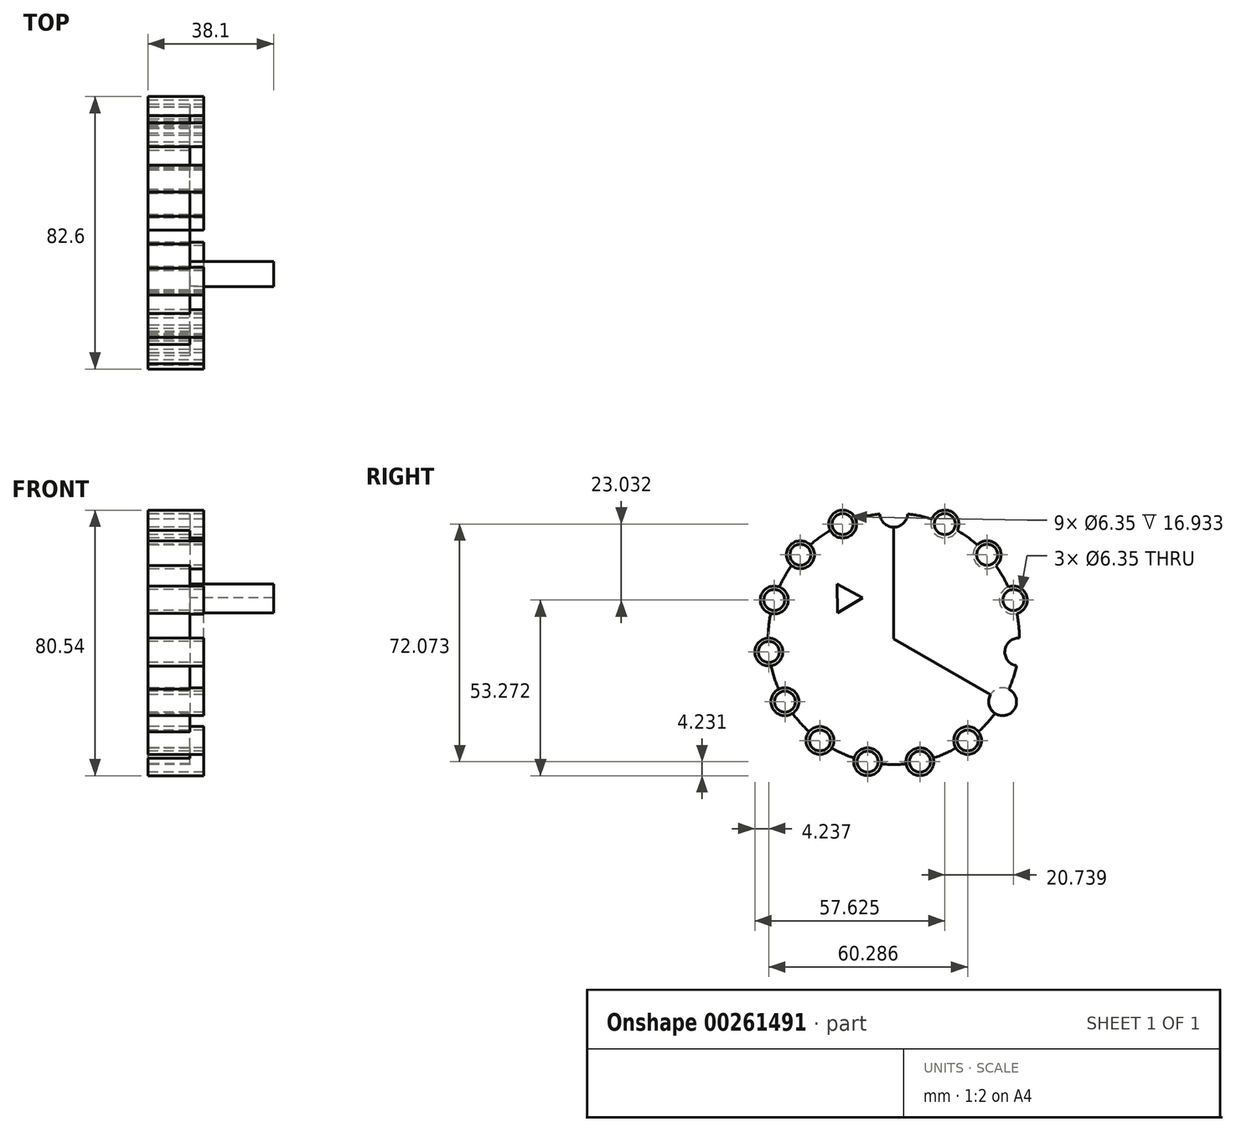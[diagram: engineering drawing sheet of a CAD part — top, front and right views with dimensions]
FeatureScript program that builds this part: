
annotation { "Feature Type Name" : "Feature", "Feature Type Description" : "" }
export const myFeature = defineFeature(function(context is Context, id is Id, definition is map)
    precondition{}
    {
        {
            var Q0;
            Q0=qCreatedBy(makeId("Right.planeOp"),FACE);
            var sketch = newSketch(context, id + "F0", { "sketchPlane" : qUnion([Q0])});
            skCircle(sketch, "E0", {"center": v(-42.41, 33.69) * mm, "radius": 38.1 * mm});
            skPoint(sketch, "E1", {"position": v(-42.41, 71.79) * mm});
            skCircle(sketch, "E2", {"center": v(-42.41, 71.79) * mm, "radius": 4.23 * mm});
            skLineSegment(sketch, "E3", {"start": v(-42.41, 33.69) * mm, "end": v(-42.41, 71.79) * mm});
            skLineSegment(sketch, "E4", {"start": v(-42.41, 33.69) * mm, "end": v(-9.42, 14.64) * mm});
            skLineSegment(sketch, "E5.MirrorCS", {"start": v(-42.41, 33.69) * mm, "end": v(-75.4, 14.64) * mm, "construction": true});
            skCircle(sketch, "E6.1.0", {"center": v(-26.91, 68.5) * mm, "radius": 4.23 * mm});
            skCircle(sketch, "E6.2.0", {"center": v(-14.1, 59.18) * mm, "radius": 4.23 * mm});
            skCircle(sketch, "E6.3.0", {"center": v(-6.18, 45.46) * mm, "radius": 4.23 * mm});
            skCircle(sketch, "E6.4.0", {"center": v(-4.52, 29.7) * mm, "radius": 4.23 * mm});
            skCircle(sketch, "E6.5.0", {"center": v(-9.42, 14.64) * mm, "radius": 4.23 * mm});
            skLineSegment(sketch, "E6.anchor1", {"start": v(-42.41, 33.69) * mm, "end": v(-42.41, 71.79) * mm, "construction": true});
            skCircle(sketch, "E7.1.0", {"center": v(-20.02, 2.86) * mm, "radius": 4.23 * mm});
            skCircle(sketch, "E7.2.0", {"center": v(-34.49, -3.58) * mm, "radius": 4.23 * mm});
            skCircle(sketch, "E7.3.0", {"center": v(-50.33, -3.58) * mm, "radius": 4.23 * mm});
            skCircle(sketch, "E7.4.0", {"center": v(-64.8, 2.86) * mm, "radius": 4.23 * mm});
            skCircle(sketch, "E7.5.0", {"center": v(-75.4, 14.64) * mm, "radius": 4.23 * mm});
            skCircle(sketch, "E8.1.0", {"center": v(-80.3, 29.7) * mm, "radius": 4.23 * mm});
            skCircle(sketch, "E8.2.0", {"center": v(-78.65, 45.46) * mm, "radius": 4.23 * mm});
            skCircle(sketch, "E8.3.0", {"center": v(-70.73, 59.18) * mm, "radius": 4.23 * mm});
            skCircle(sketch, "E8.4.0", {"center": v(-57.9, 68.5) * mm, "radius": 4.23 * mm});
            skCircle(sketch, "E9.cCircle", {"center": v(-56.97, 46.02) * mm, "radius": 2.54 * mm, "construction": true});
            skLineSegment(sketch, "E9.0", {"start": v(-59.6, 50.36) * mm, "end": v(-51.89, 46.12) * mm});
            skLineSegment(sketch, "E9.1", {"start": v(-51.89, 46.12) * mm, "end": v(-59.41, 41.57) * mm});
            skLineSegment(sketch, "E9.2", {"start": v(-59.41, 41.57) * mm, "end": v(-59.6, 50.36) * mm});
            skPoint(sketch, "E9.0.midPoint", {"position": v(-55.74, 48.24) * mm});
            skCircle(sketch, "E10", {"center": v(-6.18, 45.46) * mm, "radius": 3.18 * mm});
            skCircle(sketch, "E11.1.0", {"center": v(-4.52, 29.7) * mm, "radius": 3.18 * mm});
            skCircle(sketch, "E11.2.0", {"center": v(-9.42, 14.64) * mm, "radius": 3.17 * mm});
            skCircle(sketch, "E11.3.0", {"center": v(-20.02, 2.86) * mm, "radius": 3.18 * mm});
            skCircle(sketch, "E11.4.0", {"center": v(-34.49, -3.58) * mm, "radius": 3.18 * mm});
            skCircle(sketch, "E11.5.0", {"center": v(-50.33, -3.58) * mm, "radius": 3.18 * mm});
            skLineSegment(sketch, "E11.anchor1", {"start": v(-42.41, 33.69) * mm, "end": v(-6.18, 45.46) * mm, "construction": true});
            skLineSegment(sketch, "E11.anchor2", {"start": v(-42.41, 33.69) * mm, "end": v(-50.33, -3.58) * mm, "construction": true});
            skCircle(sketch, "E12.1.0", {"center": v(-64.8, 2.86) * mm, "radius": 3.18 * mm});
            skCircle(sketch, "E12.2.0", {"center": v(-75.4, 14.64) * mm, "radius": 3.17 * mm});
            skCircle(sketch, "E12.3.0", {"center": v(-80.3, 29.7) * mm, "radius": 3.18 * mm});
            skCircle(sketch, "E12.4.0", {"center": v(-78.65, 45.46) * mm, "radius": 3.18 * mm});
            skCircle(sketch, "E12.5.0", {"center": v(-70.73, 59.18) * mm, "radius": 3.18 * mm});
            skLineSegment(sketch, "E12.anchor2", {"start": v(-42.41, 33.69) * mm, "end": v(-70.73, 59.18) * mm, "construction": true});
            skCircle(sketch, "E13.1.0", {"center": v(-57.9, 68.5) * mm, "radius": 3.18 * mm});
            skCircle(sketch, "E13.2.0", {"center": v(-42.41, 71.79) * mm, "radius": 3.17 * mm});
            skCircle(sketch, "E13.3.0", {"center": v(-26.91, 68.5) * mm, "radius": 3.18 * mm});
            skCircle(sketch, "E13.4.0", {"center": v(-14.1, 59.18) * mm, "radius": 3.18 * mm});
            skSolve(sketch);
        }
        {
            var Q0;
            Q0=makeQuery(id+"F0.imprint","IMPRINT",FACE,{"disambiguationData":[TD([[makeQuery(id+"F0.imprint","IMPRINT",EDGE,{"derivedFrom":sQuery(id+"F0.wireOp",EDGE,"E9.0")}),1.0]])]});
            var Q1;
            {var subQ1=sQuery(id+"F0.wireOp",EDGE,"E0");var subQ4=sQuery(id+"F0.wireOp",EDGE,"E6.3.0");var subQ5=makeQuery(id+"F0.imprint","INTERSECT",VERTEX,{"disambiguationData":[OD(0.0)],"derivedFrom":[subQ1,subQ4]});Q1=makeQuery(id+"F0.imprint","IMPRINT",FACE,{"disambiguationData":[TD([[makeQuery(id+"F0.imprint","IMPRINT",EDGE,{"disambiguationData":[TD([[subQ5,1.0]])],"derivedFrom":subQ1}),1.0]])]});}
            extrude(context, id + "F1", {"entities" : qUnion([Q0, Q1]), "depth" : 12.7 * mm});
        }
        {
            var Q0;
            {var subQ0=sQuery(id+"F0.wireOp",EDGE,"E6.4.0");var subQ1=sQuery(id+"F0.wireOp",EDGE,"E0");var subQ2=makeQuery(id+"F0.imprint","INTERSECT",VERTEX,{"disambiguationData":[OD(1.0)],"derivedFrom":[subQ1,subQ0]});Q0=makeQuery(id+"F0.imprint","IMPRINT",FACE,{"disambiguationData":[TD([[makeQuery(id+"F0.imprint","IMPRINT",EDGE,{"disambiguationData":[TD([[subQ2,-1.0]])],"derivedFrom":subQ1}),1.0]])]});}
            var Q1;
            {var subQ0=sQuery(id+"F0.wireOp",EDGE,"E7.2.0");var subQ1=sQuery(id+"F0.wireOp",EDGE,"E0");var subQ2=makeQuery(id+"F0.imprint","INTERSECT",VERTEX,{"disambiguationData":[OD(0.0)],"derivedFrom":[subQ1,subQ0]});Q1=makeQuery(id+"F0.imprint","IMPRINT",FACE,{"disambiguationData":[TD([[makeQuery(id+"F0.imprint","IMPRINT",EDGE,{"disambiguationData":[TD([[subQ2,-1.0]])],"derivedFrom":subQ1}),-1.0]])]});}
            var Q2;
            {var subQ0=sQuery(id+"F0.wireOp",EDGE,"E8.1.0");var subQ1=sQuery(id+"F0.wireOp",EDGE,"E0");var subQ2=makeQuery(id+"F0.imprint","INTERSECT",VERTEX,{"disambiguationData":[OD(0.0)],"derivedFrom":[subQ1,subQ0]});Q2=makeQuery(id+"F0.imprint","IMPRINT",FACE,{"disambiguationData":[TD([[makeQuery(id+"F0.imprint","IMPRINT",EDGE,{"disambiguationData":[TD([[subQ2,-1.0]])],"derivedFrom":subQ1}),1.0]])]});}
            var Q3;
            {var subQ0=sQuery(id+"F0.wireOp",EDGE,"E6.1.0");var subQ1=sQuery(id+"F0.wireOp",EDGE,"E0");var subQ2=makeQuery(id+"F0.imprint","INTERSECT",VERTEX,{"disambiguationData":[OD(0.0)],"derivedFrom":[subQ1,subQ0]});Q3=makeQuery(id+"F0.imprint","IMPRINT",FACE,{"disambiguationData":[TD([[makeQuery(id+"F0.imprint","IMPRINT",EDGE,{"disambiguationData":[TD([[subQ2,-1.0]])],"derivedFrom":subQ1}),-1.0]])]});}
            var Q4;
            {var subQ0=sQuery(id+"F0.wireOp",EDGE,"E8.3.0");var subQ1=sQuery(id+"F0.wireOp",EDGE,"E0");var subQ2=makeQuery(id+"F0.imprint","INTERSECT",VERTEX,{"disambiguationData":[OD(0.0)],"derivedFrom":[subQ1,subQ0]});Q4=makeQuery(id+"F0.imprint","IMPRINT",FACE,{"disambiguationData":[TD([[makeQuery(id+"F0.imprint","IMPRINT",EDGE,{"disambiguationData":[TD([[subQ2,-1.0]])],"derivedFrom":subQ1}),1.0]])]});}
            var Q5;
            {var subQ0=sQuery(id+"F0.wireOp",EDGE,"E7.4.0");var subQ1=sQuery(id+"F0.wireOp",EDGE,"E0");var subQ2=makeQuery(id+"F0.imprint","INTERSECT",VERTEX,{"disambiguationData":[OD(0.0)],"derivedFrom":[subQ1,subQ0]});Q5=makeQuery(id+"F0.imprint","IMPRINT",FACE,{"disambiguationData":[TD([[makeQuery(id+"F0.imprint","IMPRINT",EDGE,{"disambiguationData":[TD([[subQ2,-1.0]])],"derivedFrom":subQ1}),1.0]])]});}
            var Q6;
            {var subQ0=sQuery(id+"F0.wireOp",EDGE,"E12.1.0");var subQ1=sQuery(id+"F0.wireOp",EDGE,"E0");var subQ2=makeQuery(id+"F0.imprint","INTERSECT",VERTEX,{"disambiguationData":[OD(0.0)],"derivedFrom":[subQ1,subQ0]});Q6=makeQuery(id+"F0.imprint","IMPRINT",FACE,{"disambiguationData":[TD([[makeQuery(id+"F0.imprint","IMPRINT",EDGE,{"disambiguationData":[TD([[subQ2,-1.0]])],"derivedFrom":subQ1}),1.0]])]});}
            var Q7;
            {var subQ0=sQuery(id+"F0.wireOp",EDGE,"E6.2.0");var subQ1=sQuery(id+"F0.wireOp",EDGE,"E0");var subQ2=makeQuery(id+"F0.imprint","INTERSECT",VERTEX,{"disambiguationData":[OD(0.0)],"derivedFrom":[subQ1,subQ0]});Q7=makeQuery(id+"F0.imprint","IMPRINT",FACE,{"disambiguationData":[TD([[makeQuery(id+"F0.imprint","IMPRINT",EDGE,{"disambiguationData":[TD([[subQ2,-1.0]])],"derivedFrom":subQ1}),-1.0]])]});}
            var Q8;
            {var subQ0=sQuery(id+"F0.wireOp",EDGE,"E6.5.0");var subQ1=sQuery(id+"F0.wireOp",EDGE,"E0");var subQ2=makeQuery(id+"F0.imprint","INTERSECT",VERTEX,{"disambiguationData":[OD(0.0)],"derivedFrom":[subQ1,subQ0]});Q8=makeQuery(id+"F0.imprint","IMPRINT",FACE,{"disambiguationData":[TD([[makeQuery(id+"F0.imprint","IMPRINT",EDGE,{"disambiguationData":[TD([[subQ2,-1.0]])],"derivedFrom":subQ1}),1.0]])]});}
            var Q9;
            {var subQ0=sQuery(id+"F0.wireOp",EDGE,"E6.4.0");var subQ1=sQuery(id+"F0.wireOp",EDGE,"E0");var subQ2=makeQuery(id+"F0.imprint","INTERSECT",VERTEX,{"disambiguationData":[OD(1.0)],"derivedFrom":[subQ1,subQ0]});Q9=makeQuery(id+"F0.imprint","IMPRINT",FACE,{"disambiguationData":[TD([[makeQuery(id+"F0.imprint","IMPRINT",EDGE,{"disambiguationData":[TD([[subQ2,-1.0]])],"derivedFrom":subQ1}),-1.0]])]});}
            var Q10;
            {var subQ0=sQuery(id+"F0.wireOp",EDGE,"E8.2.0");var subQ1=sQuery(id+"F0.wireOp",EDGE,"E0");var subQ2=makeQuery(id+"F0.imprint","INTERSECT",VERTEX,{"disambiguationData":[OD(0.0)],"derivedFrom":[subQ1,subQ0]});Q10=makeQuery(id+"F0.imprint","IMPRINT",FACE,{"disambiguationData":[TD([[makeQuery(id+"F0.imprint","IMPRINT",EDGE,{"disambiguationData":[TD([[subQ2,-1.0]])],"derivedFrom":subQ1}),1.0]])]});}
            var Q11;
            {var subQ0=sQuery(id+"F0.wireOp",EDGE,"E2");var subQ1=sQuery(id+"F0.wireOp",EDGE,"E0");var subQ2=makeQuery(id+"F0.imprint","INTERSECT",VERTEX,{"disambiguationData":[OD(0.0)],"derivedFrom":[subQ1,subQ0]});Q11=makeQuery(id+"F0.imprint","IMPRINT",FACE,{"disambiguationData":[TD([[makeQuery(id+"F0.imprint","IMPRINT",EDGE,{"disambiguationData":[TD([[subQ2,-1.0]])],"derivedFrom":subQ1}),1.0]])]});}
            var Q12;
            {var subQ0=sQuery(id+"F0.wireOp",EDGE,"E7.3.0");var subQ1=sQuery(id+"F0.wireOp",EDGE,"E0");var subQ2=makeQuery(id+"F0.imprint","INTERSECT",VERTEX,{"disambiguationData":[OD(0.0)],"derivedFrom":[subQ1,subQ0]});Q12=makeQuery(id+"F0.imprint","IMPRINT",FACE,{"disambiguationData":[TD([[makeQuery(id+"F0.imprint","IMPRINT",EDGE,{"disambiguationData":[TD([[subQ2,-1.0]])],"derivedFrom":subQ1}),1.0]])]});}
            var Q13;
            {var subQ0=sQuery(id+"F0.wireOp",EDGE,"E6.3.0");var subQ1=sQuery(id+"F0.wireOp",EDGE,"E0");var subQ2=makeQuery(id+"F0.imprint","INTERSECT",VERTEX,{"disambiguationData":[OD(0.0)],"derivedFrom":[subQ1,subQ0]});Q13=makeQuery(id+"F0.imprint","IMPRINT",FACE,{"disambiguationData":[TD([[makeQuery(id+"F0.imprint","IMPRINT",EDGE,{"disambiguationData":[TD([[subQ2,-1.0]])],"derivedFrom":subQ1}),1.0]])]});}
            var Q14;
            {var subQ0=sQuery(id+"F0.wireOp",EDGE,"E11.5.0");var subQ1=sQuery(id+"F0.wireOp",EDGE,"E0");var subQ2=makeQuery(id+"F0.imprint","INTERSECT",VERTEX,{"disambiguationData":[OD(0.0)],"derivedFrom":[subQ1,subQ0]});Q14=makeQuery(id+"F0.imprint","IMPRINT",FACE,{"disambiguationData":[TD([[makeQuery(id+"F0.imprint","IMPRINT",EDGE,{"disambiguationData":[TD([[subQ2,-1.0]])],"derivedFrom":subQ1}),1.0]])]});}
            var Q15;
            {var subQ0=sQuery(id+"F0.wireOp",EDGE,"E7.4.0");var subQ1=sQuery(id+"F0.wireOp",EDGE,"E0");var subQ2=makeQuery(id+"F0.imprint","INTERSECT",VERTEX,{"disambiguationData":[OD(0.0)],"derivedFrom":[subQ1,subQ0]});Q15=makeQuery(id+"F0.imprint","IMPRINT",FACE,{"disambiguationData":[TD([[makeQuery(id+"F0.imprint","IMPRINT",EDGE,{"disambiguationData":[TD([[subQ2,-1.0]])],"derivedFrom":subQ1}),-1.0]])]});}
            var Q16;
            {var subQ0=sQuery(id+"F0.wireOp",EDGE,"E8.1.0");var subQ1=sQuery(id+"F0.wireOp",EDGE,"E0");var subQ2=makeQuery(id+"F0.imprint","INTERSECT",VERTEX,{"disambiguationData":[OD(0.0)],"derivedFrom":[subQ1,subQ0]});Q16=makeQuery(id+"F0.imprint","IMPRINT",FACE,{"disambiguationData":[TD([[makeQuery(id+"F0.imprint","IMPRINT",EDGE,{"disambiguationData":[TD([[subQ2,-1.0]])],"derivedFrom":subQ1}),-1.0]])]});}
            var Q17;
            {var subQ0=sQuery(id+"F0.wireOp",EDGE,"E11.1.0");var subQ1=sQuery(id+"F0.wireOp",EDGE,"E0");var subQ2=makeQuery(id+"F0.imprint","INTERSECT",VERTEX,{"disambiguationData":[OD(0.0)],"derivedFrom":[subQ1,subQ0]});Q17=makeQuery(id+"F0.imprint","IMPRINT",FACE,{"disambiguationData":[TD([[makeQuery(id+"F0.imprint","IMPRINT",EDGE,{"disambiguationData":[TD([[subQ2,-1.0]])],"derivedFrom":subQ1}),1.0]])]});}
            var Q18;
            {var subQ0=sQuery(id+"F0.wireOp",EDGE,"E8.3.0");var subQ1=sQuery(id+"F0.wireOp",EDGE,"E0");var subQ2=makeQuery(id+"F0.imprint","INTERSECT",VERTEX,{"disambiguationData":[OD(0.0)],"derivedFrom":[subQ1,subQ0]});Q18=makeQuery(id+"F0.imprint","IMPRINT",FACE,{"disambiguationData":[TD([[makeQuery(id+"F0.imprint","IMPRINT",EDGE,{"disambiguationData":[TD([[subQ2,-1.0]])],"derivedFrom":subQ1}),-1.0]])]});}
            var Q19;
            {var subQ0=sQuery(id+"F0.wireOp",EDGE,"E7.2.0");var subQ1=sQuery(id+"F0.wireOp",EDGE,"E0");var subQ2=makeQuery(id+"F0.imprint","INTERSECT",VERTEX,{"disambiguationData":[OD(0.0)],"derivedFrom":[subQ1,subQ0]});Q19=makeQuery(id+"F0.imprint","IMPRINT",FACE,{"disambiguationData":[TD([[makeQuery(id+"F0.imprint","IMPRINT",EDGE,{"disambiguationData":[TD([[subQ2,-1.0]])],"derivedFrom":subQ1}),1.0]])]});}
            var Q20;
            {var subQ0=sQuery(id+"F0.wireOp",EDGE,"E7.5.0");var subQ1=sQuery(id+"F0.wireOp",EDGE,"E0");var subQ2=makeQuery(id+"F0.imprint","INTERSECT",VERTEX,{"disambiguationData":[OD(0.0)],"derivedFrom":[subQ1,subQ0]});Q20=makeQuery(id+"F0.imprint","IMPRINT",FACE,{"disambiguationData":[TD([[makeQuery(id+"F0.imprint","IMPRINT",EDGE,{"disambiguationData":[TD([[subQ2,-1.0]])],"derivedFrom":subQ1}),1.0]])]});}
            var Q21;
            {var subQ0=sQuery(id+"F0.wireOp",EDGE,"E12.3.0");var subQ1=sQuery(id+"F0.wireOp",EDGE,"E0");var subQ2=makeQuery(id+"F0.imprint","INTERSECT",VERTEX,{"disambiguationData":[OD(0.0)],"derivedFrom":[subQ1,subQ0]});Q21=makeQuery(id+"F0.imprint","IMPRINT",FACE,{"disambiguationData":[TD([[makeQuery(id+"F0.imprint","IMPRINT",EDGE,{"disambiguationData":[TD([[subQ2,-1.0]])],"derivedFrom":subQ1}),1.0]])]});}
            var Q22;
            {var subQ0=sQuery(id+"F0.wireOp",EDGE,"E13.1.0");var subQ1=sQuery(id+"F0.wireOp",EDGE,"E0");var subQ2=makeQuery(id+"F0.imprint","INTERSECT",VERTEX,{"disambiguationData":[OD(0.0)],"derivedFrom":[subQ1,subQ0]});Q22=makeQuery(id+"F0.imprint","IMPRINT",FACE,{"disambiguationData":[TD([[makeQuery(id+"F0.imprint","IMPRINT",EDGE,{"disambiguationData":[TD([[subQ2,-1.0]])],"derivedFrom":subQ1}),1.0]])]});}
            var Q23;
            {var subQ0=sQuery(id+"F0.wireOp",EDGE,"E6.1.0");var subQ1=sQuery(id+"F0.wireOp",EDGE,"E0");var subQ2=makeQuery(id+"F0.imprint","INTERSECT",VERTEX,{"disambiguationData":[OD(0.0)],"derivedFrom":[subQ1,subQ0]});Q23=makeQuery(id+"F0.imprint","IMPRINT",FACE,{"disambiguationData":[TD([[makeQuery(id+"F0.imprint","IMPRINT",EDGE,{"disambiguationData":[TD([[subQ2,-1.0]])],"derivedFrom":subQ1}),1.0]])]});}
            var Q24;
            {var subQ0=sQuery(id+"F0.wireOp",EDGE,"E7.3.0");var subQ1=sQuery(id+"F0.wireOp",EDGE,"E0");var subQ2=makeQuery(id+"F0.imprint","INTERSECT",VERTEX,{"disambiguationData":[OD(0.0)],"derivedFrom":[subQ1,subQ0]});Q24=makeQuery(id+"F0.imprint","IMPRINT",FACE,{"disambiguationData":[TD([[makeQuery(id+"F0.imprint","IMPRINT",EDGE,{"disambiguationData":[TD([[subQ2,-1.0]])],"derivedFrom":subQ1}),-1.0]])]});}
            var Q25;
            {var subQ0=sQuery(id+"F0.wireOp",EDGE,"E12.1.0");var subQ1=sQuery(id+"F0.wireOp",EDGE,"E0");var subQ2=makeQuery(id+"F0.imprint","INTERSECT",VERTEX,{"disambiguationData":[OD(0.0)],"derivedFrom":[subQ1,subQ0]});Q25=makeQuery(id+"F0.imprint","IMPRINT",FACE,{"disambiguationData":[TD([[makeQuery(id+"F0.imprint","IMPRINT",EDGE,{"disambiguationData":[TD([[subQ2,-1.0]])],"derivedFrom":subQ1}),-1.0]])]});}
            var Q26;
            {var subQ0=sQuery(id+"F0.wireOp",EDGE,"E6.2.0");var subQ1=sQuery(id+"F0.wireOp",EDGE,"E0");var subQ2=makeQuery(id+"F0.imprint","INTERSECT",VERTEX,{"disambiguationData":[OD(0.0)],"derivedFrom":[subQ1,subQ0]});Q26=makeQuery(id+"F0.imprint","IMPRINT",FACE,{"disambiguationData":[TD([[makeQuery(id+"F0.imprint","IMPRINT",EDGE,{"disambiguationData":[TD([[subQ2,-1.0]])],"derivedFrom":subQ1}),1.0]])]});}
            var Q27;
            {var subQ0=sQuery(id+"F0.wireOp",EDGE,"E7.1.0");var subQ1=sQuery(id+"F0.wireOp",EDGE,"E0");var subQ2=makeQuery(id+"F0.imprint","INTERSECT",VERTEX,{"disambiguationData":[OD(0.0)],"derivedFrom":[subQ1,subQ0]});Q27=makeQuery(id+"F0.imprint","IMPRINT",FACE,{"disambiguationData":[TD([[makeQuery(id+"F0.imprint","IMPRINT",EDGE,{"disambiguationData":[TD([[subQ2,-1.0]])],"derivedFrom":subQ1}),-1.0]])]});}
            var Q28;
            {var subQ0=sQuery(id+"F0.wireOp",EDGE,"E12.5.0");var subQ1=sQuery(id+"F0.wireOp",EDGE,"E0");var subQ2=makeQuery(id+"F0.imprint","INTERSECT",VERTEX,{"disambiguationData":[OD(0.0)],"derivedFrom":[subQ1,subQ0]});Q28=makeQuery(id+"F0.imprint","IMPRINT",FACE,{"disambiguationData":[TD([[makeQuery(id+"F0.imprint","IMPRINT",EDGE,{"disambiguationData":[TD([[subQ2,-1.0]])],"derivedFrom":subQ1}),-1.0]])]});}
            var Q29;
            {var subQ0=sQuery(id+"F0.wireOp",EDGE,"E7.1.0");var subQ1=sQuery(id+"F0.wireOp",EDGE,"E0");var subQ2=makeQuery(id+"F0.imprint","INTERSECT",VERTEX,{"disambiguationData":[OD(0.0)],"derivedFrom":[subQ1,subQ0]});Q29=makeQuery(id+"F0.imprint","IMPRINT",FACE,{"disambiguationData":[TD([[makeQuery(id+"F0.imprint","IMPRINT",EDGE,{"disambiguationData":[TD([[subQ2,-1.0]])],"derivedFrom":subQ1}),1.0]])]});}
            var Q30;
            {var subQ0=sQuery(id+"F0.wireOp",EDGE,"E6.3.0");var subQ1=sQuery(id+"F0.wireOp",EDGE,"E0");var subQ2=makeQuery(id+"F0.imprint","INTERSECT",VERTEX,{"disambiguationData":[OD(0.0)],"derivedFrom":[subQ1,subQ0]});Q30=makeQuery(id+"F0.imprint","IMPRINT",FACE,{"disambiguationData":[TD([[makeQuery(id+"F0.imprint","IMPRINT",EDGE,{"disambiguationData":[TD([[subQ2,-1.0]])],"derivedFrom":subQ1}),-1.0]])]});}
            var Q31;
            {var subQ0=sQuery(id+"F0.wireOp",EDGE,"E7.5.0");var subQ1=sQuery(id+"F0.wireOp",EDGE,"E0");var subQ2=makeQuery(id+"F0.imprint","INTERSECT",VERTEX,{"disambiguationData":[OD(0.0)],"derivedFrom":[subQ1,subQ0]});Q31=makeQuery(id+"F0.imprint","IMPRINT",FACE,{"disambiguationData":[TD([[makeQuery(id+"F0.imprint","IMPRINT",EDGE,{"disambiguationData":[TD([[subQ2,-1.0]])],"derivedFrom":subQ1}),-1.0]])]});}
            var Q32;
            Q32=makeQuery(id+"F0.imprint","IMPRINT",FACE,{"disambiguationData":[TD([[makeQuery(id+"F0.imprint","IMPRINT",EDGE,{"derivedFrom":sQuery(id+"F0.wireOp",EDGE,"E9.0")}),-1.0]])]});
            var Q33;
            {var subQ0=sQuery(id+"F0.wireOp",EDGE,"E8.4.0");var subQ1=sQuery(id+"F0.wireOp",EDGE,"E0");var subQ2=makeQuery(id+"F0.imprint","INTERSECT",VERTEX,{"disambiguationData":[OD(0.0)],"derivedFrom":[subQ1,subQ0]});Q33=makeQuery(id+"F0.imprint","IMPRINT",FACE,{"disambiguationData":[TD([[makeQuery(id+"F0.imprint","IMPRINT",EDGE,{"disambiguationData":[TD([[subQ2,-1.0]])],"derivedFrom":subQ1}),-1.0]])]});}
            var Q34;
            {var subQ0=sQuery(id+"F0.wireOp",EDGE,"E6.5.0");var subQ1=sQuery(id+"F0.wireOp",EDGE,"E0");var subQ2=makeQuery(id+"F0.imprint","INTERSECT",VERTEX,{"disambiguationData":[OD(0.0)],"derivedFrom":[subQ1,subQ0]});Q34=makeQuery(id+"F0.imprint","IMPRINT",FACE,{"disambiguationData":[TD([[makeQuery(id+"F0.imprint","IMPRINT",EDGE,{"disambiguationData":[TD([[subQ2,-1.0]])],"derivedFrom":subQ1}),-1.0]])]});}
            var Q35;
            {var subQ0=sQuery(id+"F0.wireOp",EDGE,"E11.5.0");var subQ1=sQuery(id+"F0.wireOp",EDGE,"E0");var subQ2=makeQuery(id+"F0.imprint","INTERSECT",VERTEX,{"disambiguationData":[OD(0.0)],"derivedFrom":[subQ1,subQ0]});Q35=makeQuery(id+"F0.imprint","IMPRINT",FACE,{"disambiguationData":[TD([[makeQuery(id+"F0.imprint","IMPRINT",EDGE,{"disambiguationData":[TD([[subQ2,-1.0]])],"derivedFrom":subQ1}),-1.0]])]});}
            var Q36;
            {var subQ0=sQuery(id+"F0.wireOp",EDGE,"E6.5.0");var subQ1=sQuery(id+"F0.wireOp",EDGE,"E0");var subQ2=makeQuery(id+"F0.imprint","INTERSECT",VERTEX,{"disambiguationData":[OD(1.0)],"derivedFrom":[subQ1,subQ0]});Q36=makeQuery(id+"F0.imprint","IMPRINT",FACE,{"disambiguationData":[TD([[makeQuery(id+"F0.imprint","IMPRINT",EDGE,{"disambiguationData":[TD([[subQ2,1.0]])],"derivedFrom":subQ1}),1.0]])]});}
            var Q37;
            {var subQ0=sQuery(id+"F0.wireOp",EDGE,"E8.2.0");var subQ1=sQuery(id+"F0.wireOp",EDGE,"E0");var subQ2=makeQuery(id+"F0.imprint","INTERSECT",VERTEX,{"disambiguationData":[OD(0.0)],"derivedFrom":[subQ1,subQ0]});Q37=makeQuery(id+"F0.imprint","IMPRINT",FACE,{"disambiguationData":[TD([[makeQuery(id+"F0.imprint","IMPRINT",EDGE,{"disambiguationData":[TD([[subQ2,-1.0]])],"derivedFrom":subQ1}),-1.0]])]});}
            var Q38;
            {var subQ0=sQuery(id+"F0.wireOp",EDGE,"E8.4.0");var subQ1=sQuery(id+"F0.wireOp",EDGE,"E0");var subQ2=makeQuery(id+"F0.imprint","INTERSECT",VERTEX,{"disambiguationData":[OD(0.0)],"derivedFrom":[subQ1,subQ0]});Q38=makeQuery(id+"F0.imprint","IMPRINT",FACE,{"disambiguationData":[TD([[makeQuery(id+"F0.imprint","IMPRINT",EDGE,{"disambiguationData":[TD([[subQ2,-1.0]])],"derivedFrom":subQ1}),1.0]])]});}
            var Q39;
            {var subQ0=sQuery(id+"F0.wireOp",EDGE,"E13.4.0");var subQ1=sQuery(id+"F0.wireOp",EDGE,"E0");var subQ2=makeQuery(id+"F0.imprint","INTERSECT",VERTEX,{"disambiguationData":[OD(0.0)],"derivedFrom":[subQ1,subQ0]});Q39=makeQuery(id+"F0.imprint","IMPRINT",FACE,{"disambiguationData":[TD([[makeQuery(id+"F0.imprint","IMPRINT",EDGE,{"disambiguationData":[TD([[subQ2,-1.0]])],"derivedFrom":subQ1}),-1.0]])]});}
            var Q40;
            {var subQ0=sQuery(id+"F0.wireOp",EDGE,"E13.3.0");var subQ1=sQuery(id+"F0.wireOp",EDGE,"E0");var subQ2=makeQuery(id+"F0.imprint","INTERSECT",VERTEX,{"disambiguationData":[OD(0.0)],"derivedFrom":[subQ1,subQ0]});Q40=makeQuery(id+"F0.imprint","IMPRINT",FACE,{"disambiguationData":[TD([[makeQuery(id+"F0.imprint","IMPRINT",EDGE,{"disambiguationData":[TD([[subQ2,-1.0]])],"derivedFrom":subQ1}),1.0]])]});}
            var Q41;
            {var subQ0=sQuery(id+"F0.wireOp",EDGE,"E10");var subQ1=sQuery(id+"F0.wireOp",EDGE,"E0");var subQ2=makeQuery(id+"F0.imprint","INTERSECT",VERTEX,{"disambiguationData":[OD(0.0)],"derivedFrom":[subQ1,subQ0]});Q41=makeQuery(id+"F0.imprint","IMPRINT",FACE,{"disambiguationData":[TD([[makeQuery(id+"F0.imprint","IMPRINT",EDGE,{"disambiguationData":[TD([[subQ2,-1.0]])],"derivedFrom":subQ1}),-1.0]])]});}
            var Q42;
            {var subQ0=sQuery(id+"F0.wireOp",EDGE,"E11.3.0");var subQ1=sQuery(id+"F0.wireOp",EDGE,"E0");var subQ2=makeQuery(id+"F0.imprint","INTERSECT",VERTEX,{"disambiguationData":[OD(0.0)],"derivedFrom":[subQ1,subQ0]});Q42=makeQuery(id+"F0.imprint","IMPRINT",FACE,{"disambiguationData":[TD([[makeQuery(id+"F0.imprint","IMPRINT",EDGE,{"disambiguationData":[TD([[subQ2,-1.0]])],"derivedFrom":subQ1}),-1.0]])]});}
            var Q43;
            {var subQ0=sQuery(id+"F0.wireOp",EDGE,"E11.1.0");var subQ1=sQuery(id+"F0.wireOp",EDGE,"E0");var subQ2=makeQuery(id+"F0.imprint","INTERSECT",VERTEX,{"disambiguationData":[OD(0.0)],"derivedFrom":[subQ1,subQ0]});Q43=makeQuery(id+"F0.imprint","IMPRINT",FACE,{"disambiguationData":[TD([[makeQuery(id+"F0.imprint","IMPRINT",EDGE,{"disambiguationData":[TD([[subQ2,-1.0]])],"derivedFrom":subQ1}),-1.0]])]});}
            var Q44;
            {var subQ0=sQuery(id+"F0.wireOp",EDGE,"E11.3.0");var subQ1=sQuery(id+"F0.wireOp",EDGE,"E0");var subQ2=makeQuery(id+"F0.imprint","INTERSECT",VERTEX,{"disambiguationData":[OD(0.0)],"derivedFrom":[subQ1,subQ0]});Q44=makeQuery(id+"F0.imprint","IMPRINT",FACE,{"disambiguationData":[TD([[makeQuery(id+"F0.imprint","IMPRINT",EDGE,{"disambiguationData":[TD([[subQ2,-1.0]])],"derivedFrom":subQ1}),1.0]])]});}
            var Q45;
            {var subQ0=sQuery(id+"F0.wireOp",EDGE,"E2");var subQ1=sQuery(id+"F0.wireOp",EDGE,"E0");var subQ2=makeQuery(id+"F0.imprint","INTERSECT",VERTEX,{"disambiguationData":[OD(1.0)],"derivedFrom":[subQ1,subQ0]});Q45=makeQuery(id+"F0.imprint","IMPRINT",FACE,{"disambiguationData":[TD([[makeQuery(id+"F0.imprint","IMPRINT",EDGE,{"disambiguationData":[TD([[subQ2,1.0]])],"derivedFrom":subQ1}),1.0]])]});}
            var Q46;
            {var subQ0=sQuery(id+"F0.wireOp",EDGE,"E2");var subQ1=sQuery(id+"F0.wireOp",EDGE,"E0");var subQ2=makeQuery(id+"F0.imprint","INTERSECT",VERTEX,{"disambiguationData":[OD(0.0)],"derivedFrom":[subQ1,subQ0]});Q46=makeQuery(id+"F0.imprint","IMPRINT",FACE,{"disambiguationData":[TD([[makeQuery(id+"F0.imprint","IMPRINT",EDGE,{"disambiguationData":[TD([[subQ2,-1.0]])],"derivedFrom":subQ1}),-1.0]])]});}
            var Q47;
            {var subQ0=sQuery(id+"F0.wireOp",EDGE,"E12.4.0");var subQ1=sQuery(id+"F0.wireOp",EDGE,"E0");var subQ2=makeQuery(id+"F0.imprint","INTERSECT",VERTEX,{"disambiguationData":[OD(0.0)],"derivedFrom":[subQ1,subQ0]});Q47=makeQuery(id+"F0.imprint","IMPRINT",FACE,{"disambiguationData":[TD([[makeQuery(id+"F0.imprint","IMPRINT",EDGE,{"disambiguationData":[TD([[subQ2,-1.0]])],"derivedFrom":subQ1}),-1.0]])]});}
            var Q48;
            {var subQ0=sQuery(id+"F0.wireOp",EDGE,"E13.1.0");var subQ1=sQuery(id+"F0.wireOp",EDGE,"E0");var subQ2=makeQuery(id+"F0.imprint","INTERSECT",VERTEX,{"disambiguationData":[OD(0.0)],"derivedFrom":[subQ1,subQ0]});Q48=makeQuery(id+"F0.imprint","IMPRINT",FACE,{"disambiguationData":[TD([[makeQuery(id+"F0.imprint","IMPRINT",EDGE,{"disambiguationData":[TD([[subQ2,-1.0]])],"derivedFrom":subQ1}),-1.0]])]});}
            var Q49;
            {var subQ0=sQuery(id+"F0.wireOp",EDGE,"E12.2.0");var subQ1=sQuery(id+"F0.wireOp",EDGE,"E0");var subQ2=makeQuery(id+"F0.imprint","INTERSECT",VERTEX,{"disambiguationData":[OD(0.0)],"derivedFrom":[subQ1,subQ0]});Q49=makeQuery(id+"F0.imprint","IMPRINT",FACE,{"disambiguationData":[TD([[makeQuery(id+"F0.imprint","IMPRINT",EDGE,{"disambiguationData":[TD([[subQ2,-1.0]])],"derivedFrom":subQ1}),1.0]])]});}
            var Q50;
            {var subQ0=sQuery(id+"F0.wireOp",EDGE,"E0");var subQ1=makeQuery(id+"F0.imprint","INTERSECT",VERTEX,{"derivedFrom":[subQ0,sQuery(id+"F0.wireOp",EDGE,"E4")]});Q50=makeQuery(id+"F0.imprint","IMPRINT",FACE,{"disambiguationData":[TD([[makeQuery(id+"F0.imprint","IMPRINT",EDGE,{"disambiguationData":[TD([[subQ1,1.0]])],"derivedFrom":subQ0}),-1.0]])]});}
            var Q51;
            {var subQ0=sQuery(id+"F0.wireOp",EDGE,"E11.4.0");var subQ1=sQuery(id+"F0.wireOp",EDGE,"E0");var subQ2=makeQuery(id+"F0.imprint","INTERSECT",VERTEX,{"disambiguationData":[OD(0.0)],"derivedFrom":[subQ1,subQ0]});Q51=makeQuery(id+"F0.imprint","IMPRINT",FACE,{"disambiguationData":[TD([[makeQuery(id+"F0.imprint","IMPRINT",EDGE,{"disambiguationData":[TD([[subQ2,-1.0]])],"derivedFrom":subQ1}),-1.0]])]});}
            var Q52;
            {var subQ0=sQuery(id+"F0.wireOp",EDGE,"E13.4.0");var subQ1=sQuery(id+"F0.wireOp",EDGE,"E0");var subQ2=makeQuery(id+"F0.imprint","INTERSECT",VERTEX,{"disambiguationData":[OD(0.0)],"derivedFrom":[subQ1,subQ0]});Q52=makeQuery(id+"F0.imprint","IMPRINT",FACE,{"disambiguationData":[TD([[makeQuery(id+"F0.imprint","IMPRINT",EDGE,{"disambiguationData":[TD([[subQ2,-1.0]])],"derivedFrom":subQ1}),1.0]])]});}
            var Q53;
            {var subQ0=sQuery(id+"F0.wireOp",EDGE,"E4");var subQ1=sQuery(id+"F0.wireOp",EDGE,"E0");var subQ2=makeQuery(id+"F0.imprint","INTERSECT",VERTEX,{"derivedFrom":[subQ1,subQ0]});Q53=makeQuery(id+"F0.imprint","IMPRINT",FACE,{"disambiguationData":[TD([[makeQuery(id+"F0.imprint","IMPRINT",EDGE,{"disambiguationData":[TD([[subQ2,-1.0]])],"derivedFrom":subQ1}),1.0]])]});}
            var Q54;
            {var subQ0=sQuery(id+"F0.wireOp",EDGE,"E13.3.0");var subQ1=sQuery(id+"F0.wireOp",EDGE,"E0");var subQ2=makeQuery(id+"F0.imprint","INTERSECT",VERTEX,{"disambiguationData":[OD(0.0)],"derivedFrom":[subQ1,subQ0]});Q54=makeQuery(id+"F0.imprint","IMPRINT",FACE,{"disambiguationData":[TD([[makeQuery(id+"F0.imprint","IMPRINT",EDGE,{"disambiguationData":[TD([[subQ2,-1.0]])],"derivedFrom":subQ1}),-1.0]])]});}
            var Q55;
            {var subQ0=sQuery(id+"F0.wireOp",EDGE,"E11.4.0");var subQ1=sQuery(id+"F0.wireOp",EDGE,"E0");var subQ2=makeQuery(id+"F0.imprint","INTERSECT",VERTEX,{"disambiguationData":[OD(0.0)],"derivedFrom":[subQ1,subQ0]});Q55=makeQuery(id+"F0.imprint","IMPRINT",FACE,{"disambiguationData":[TD([[makeQuery(id+"F0.imprint","IMPRINT",EDGE,{"disambiguationData":[TD([[subQ2,-1.0]])],"derivedFrom":subQ1}),1.0]])]});}
            var Q56;
            {var subQ0=sQuery(id+"F0.wireOp",EDGE,"E10");var subQ1=sQuery(id+"F0.wireOp",EDGE,"E0");var subQ2=makeQuery(id+"F0.imprint","INTERSECT",VERTEX,{"disambiguationData":[OD(0.0)],"derivedFrom":[subQ1,subQ0]});Q56=makeQuery(id+"F0.imprint","IMPRINT",FACE,{"disambiguationData":[TD([[makeQuery(id+"F0.imprint","IMPRINT",EDGE,{"disambiguationData":[TD([[subQ2,-1.0]])],"derivedFrom":subQ1}),1.0]])]});}
            var Q57;
            {var subQ0=sQuery(id+"F0.wireOp",EDGE,"E12.4.0");var subQ1=sQuery(id+"F0.wireOp",EDGE,"E0");var subQ2=makeQuery(id+"F0.imprint","INTERSECT",VERTEX,{"disambiguationData":[OD(0.0)],"derivedFrom":[subQ1,subQ0]});Q57=makeQuery(id+"F0.imprint","IMPRINT",FACE,{"disambiguationData":[TD([[makeQuery(id+"F0.imprint","IMPRINT",EDGE,{"disambiguationData":[TD([[subQ2,-1.0]])],"derivedFrom":subQ1}),1.0]])]});}
            var Q58;
            {var subQ0=sQuery(id+"F0.wireOp",EDGE,"E12.3.0");var subQ1=sQuery(id+"F0.wireOp",EDGE,"E0");var subQ2=makeQuery(id+"F0.imprint","INTERSECT",VERTEX,{"disambiguationData":[OD(0.0)],"derivedFrom":[subQ1,subQ0]});Q58=makeQuery(id+"F0.imprint","IMPRINT",FACE,{"disambiguationData":[TD([[makeQuery(id+"F0.imprint","IMPRINT",EDGE,{"disambiguationData":[TD([[subQ2,-1.0]])],"derivedFrom":subQ1}),-1.0]])]});}
            var Q59;
            {var subQ0=sQuery(id+"F0.wireOp",EDGE,"E3");var subQ1=sQuery(id+"F0.wireOp",EDGE,"E0");var subQ2=makeQuery(id+"F0.imprint","INTERSECT",VERTEX,{"derivedFrom":[subQ1,subQ0]});Q59=makeQuery(id+"F0.imprint","IMPRINT",FACE,{"disambiguationData":[TD([[makeQuery(id+"F0.imprint","IMPRINT",EDGE,{"disambiguationData":[TD([[subQ2,1.0]])],"derivedFrom":subQ1}),1.0]])]});}
            var Q60;
            {var subQ0=sQuery(id+"F0.wireOp",EDGE,"E3");var subQ1=sQuery(id+"F0.wireOp",EDGE,"E0");var subQ2=makeQuery(id+"F0.imprint","INTERSECT",VERTEX,{"derivedFrom":[subQ1,subQ0]});Q60=makeQuery(id+"F0.imprint","IMPRINT",FACE,{"disambiguationData":[TD([[makeQuery(id+"F0.imprint","IMPRINT",EDGE,{"disambiguationData":[TD([[subQ2,-1.0]])],"derivedFrom":subQ1}),1.0]])]});}
            var Q61;
            {var subQ0=sQuery(id+"F0.wireOp",EDGE,"E0");var subQ1=makeQuery(id+"F0.imprint","INTERSECT",VERTEX,{"derivedFrom":[subQ0,sQuery(id+"F0.wireOp",EDGE,"E3")]});Q61=makeQuery(id+"F0.imprint","IMPRINT",FACE,{"disambiguationData":[TD([[makeQuery(id+"F0.imprint","IMPRINT",EDGE,{"disambiguationData":[TD([[subQ1,1.0]])],"derivedFrom":subQ0}),-1.0]])]});}
            var Q62;
            {var subQ0=sQuery(id+"F0.wireOp",EDGE,"E4");var subQ1=sQuery(id+"F0.wireOp",EDGE,"E0");var subQ2=makeQuery(id+"F0.imprint","INTERSECT",VERTEX,{"derivedFrom":[subQ1,subQ0]});Q62=makeQuery(id+"F0.imprint","IMPRINT",FACE,{"disambiguationData":[TD([[makeQuery(id+"F0.imprint","IMPRINT",EDGE,{"disambiguationData":[TD([[subQ2,1.0]])],"derivedFrom":subQ1}),1.0]])]});}
            var Q63;
            {var subQ0=sQuery(id+"F0.wireOp",EDGE,"E12.2.0");var subQ1=sQuery(id+"F0.wireOp",EDGE,"E0");var subQ2=makeQuery(id+"F0.imprint","INTERSECT",VERTEX,{"disambiguationData":[OD(0.0)],"derivedFrom":[subQ1,subQ0]});Q63=makeQuery(id+"F0.imprint","IMPRINT",FACE,{"disambiguationData":[TD([[makeQuery(id+"F0.imprint","IMPRINT",EDGE,{"disambiguationData":[TD([[subQ2,-1.0]])],"derivedFrom":subQ1}),-1.0]])]});}
            var Q64;
            {var subQ0=sQuery(id+"F0.wireOp",EDGE,"E12.5.0");var subQ1=sQuery(id+"F0.wireOp",EDGE,"E0");var subQ2=makeQuery(id+"F0.imprint","INTERSECT",VERTEX,{"disambiguationData":[OD(0.0)],"derivedFrom":[subQ1,subQ0]});Q64=makeQuery(id+"F0.imprint","IMPRINT",FACE,{"disambiguationData":[TD([[makeQuery(id+"F0.imprint","IMPRINT",EDGE,{"disambiguationData":[TD([[subQ2,-1.0]])],"derivedFrom":subQ1}),1.0]])]});}
            extrude(context, id + "F2", {"entities" : qUnion([Q0, Q1, Q2, Q3, Q4, Q5, Q6, Q7, Q8, Q9, Q10, Q11, Q12, Q13, Q14, Q15, Q16, Q17, Q18, Q19, Q20, Q21, Q22, Q23, Q24, Q25, Q26, Q27, Q28, Q29, Q30, Q31, Q32, Q33, Q34, Q35, Q36, Q37, Q38, Q39, Q40, Q41, Q42, Q43, Q44, Q45, Q46, Q47, Q48, Q49, Q50, Q51, Q52, Q53, Q54, Q55, Q56, Q57, Q58, Q59, Q60, Q61, Q62, Q63, Q64]), "depth" : 16.93 * mm});
        }
        {
            var Q0;
            {var subQ0=sQuery(id+"F0.wireOp",EDGE,"E13.4.0");var subQ1=sQuery(id+"F0.wireOp",EDGE,"E0");var subQ2=makeQuery(id+"F0.imprint","INTERSECT",VERTEX,{"disambiguationData":[OD(0.0)],"derivedFrom":[subQ1,subQ0]});Q0=makeQuery(id+"F0.imprint","IMPRINT",FACE,{"disambiguationData":[TD([[makeQuery(id+"F0.imprint","IMPRINT",EDGE,{"disambiguationData":[TD([[subQ2,-1.0]])],"derivedFrom":subQ1}),1.0]])]});}
            var Q1;
            {var subQ0=sQuery(id+"F0.wireOp",EDGE,"E13.4.0");var subQ1=sQuery(id+"F0.wireOp",EDGE,"E0");var subQ2=makeQuery(id+"F0.imprint","INTERSECT",VERTEX,{"disambiguationData":[OD(0.0)],"derivedFrom":[subQ1,subQ0]});Q1=makeQuery(id+"F0.imprint","IMPRINT",FACE,{"disambiguationData":[TD([[makeQuery(id+"F0.imprint","IMPRINT",EDGE,{"disambiguationData":[TD([[subQ2,-1.0]])],"derivedFrom":subQ1}),-1.0]])]});}
            var Q2;
            {var subQ0=sQuery(id+"F0.wireOp",EDGE,"E13.3.0");var subQ1=sQuery(id+"F0.wireOp",EDGE,"E0");var subQ2=makeQuery(id+"F0.imprint","INTERSECT",VERTEX,{"disambiguationData":[OD(0.0)],"derivedFrom":[subQ1,subQ0]});Q2=makeQuery(id+"F0.imprint","IMPRINT",FACE,{"disambiguationData":[TD([[makeQuery(id+"F0.imprint","IMPRINT",EDGE,{"disambiguationData":[TD([[subQ2,-1.0]])],"derivedFrom":subQ1}),-1.0]])]});}
            var Q3;
            {var subQ0=sQuery(id+"F0.wireOp",EDGE,"E13.3.0");var subQ1=sQuery(id+"F0.wireOp",EDGE,"E0");var subQ2=makeQuery(id+"F0.imprint","INTERSECT",VERTEX,{"disambiguationData":[OD(0.0)],"derivedFrom":[subQ1,subQ0]});Q3=makeQuery(id+"F0.imprint","IMPRINT",FACE,{"disambiguationData":[TD([[makeQuery(id+"F0.imprint","IMPRINT",EDGE,{"disambiguationData":[TD([[subQ2,-1.0]])],"derivedFrom":subQ1}),1.0]])]});}
            var Q4;
            {var subQ0=sQuery(id+"F0.wireOp",EDGE,"E0");var subQ1=makeQuery(id+"F0.imprint","INTERSECT",VERTEX,{"derivedFrom":[subQ0,sQuery(id+"F0.wireOp",EDGE,"E3")]});Q4=makeQuery(id+"F0.imprint","IMPRINT",FACE,{"disambiguationData":[TD([[makeQuery(id+"F0.imprint","IMPRINT",EDGE,{"disambiguationData":[TD([[subQ1,1.0]])],"derivedFrom":subQ0}),-1.0]])]});}
            var Q5;
            {var subQ0=sQuery(id+"F0.wireOp",EDGE,"E3");var subQ1=sQuery(id+"F0.wireOp",EDGE,"E0");var subQ2=makeQuery(id+"F0.imprint","INTERSECT",VERTEX,{"derivedFrom":[subQ1,subQ0]});Q5=makeQuery(id+"F0.imprint","IMPRINT",FACE,{"disambiguationData":[TD([[makeQuery(id+"F0.imprint","IMPRINT",EDGE,{"disambiguationData":[TD([[subQ2,-1.0]])],"derivedFrom":subQ1}),1.0]])]});}
            var Q6;
            {var subQ0=sQuery(id+"F0.wireOp",EDGE,"E3");var subQ1=sQuery(id+"F0.wireOp",EDGE,"E0");var subQ2=makeQuery(id+"F0.imprint","INTERSECT",VERTEX,{"derivedFrom":[subQ1,subQ0]});Q6=makeQuery(id+"F0.imprint","IMPRINT",FACE,{"disambiguationData":[TD([[makeQuery(id+"F0.imprint","IMPRINT",EDGE,{"disambiguationData":[TD([[subQ2,1.0]])],"derivedFrom":subQ1}),1.0]])]});}
            var Q7;
            {var subQ0=sQuery(id+"F0.wireOp",EDGE,"E13.1.0");var subQ1=sQuery(id+"F0.wireOp",EDGE,"E0");var subQ2=makeQuery(id+"F0.imprint","INTERSECT",VERTEX,{"disambiguationData":[OD(0.0)],"derivedFrom":[subQ1,subQ0]});Q7=makeQuery(id+"F0.imprint","IMPRINT",FACE,{"disambiguationData":[TD([[makeQuery(id+"F0.imprint","IMPRINT",EDGE,{"disambiguationData":[TD([[subQ2,-1.0]])],"derivedFrom":subQ1}),-1.0]])]});}
            var Q8;
            {var subQ0=sQuery(id+"F0.wireOp",EDGE,"E13.1.0");var subQ1=sQuery(id+"F0.wireOp",EDGE,"E0");var subQ2=makeQuery(id+"F0.imprint","INTERSECT",VERTEX,{"disambiguationData":[OD(0.0)],"derivedFrom":[subQ1,subQ0]});Q8=makeQuery(id+"F0.imprint","IMPRINT",FACE,{"disambiguationData":[TD([[makeQuery(id+"F0.imprint","IMPRINT",EDGE,{"disambiguationData":[TD([[subQ2,-1.0]])],"derivedFrom":subQ1}),1.0]])]});}
            var Q9;
            {var subQ0=sQuery(id+"F0.wireOp",EDGE,"E12.5.0");var subQ1=sQuery(id+"F0.wireOp",EDGE,"E0");var subQ2=makeQuery(id+"F0.imprint","INTERSECT",VERTEX,{"disambiguationData":[OD(0.0)],"derivedFrom":[subQ1,subQ0]});Q9=makeQuery(id+"F0.imprint","IMPRINT",FACE,{"disambiguationData":[TD([[makeQuery(id+"F0.imprint","IMPRINT",EDGE,{"disambiguationData":[TD([[subQ2,-1.0]])],"derivedFrom":subQ1}),-1.0]])]});}
            var Q10;
            {var subQ0=sQuery(id+"F0.wireOp",EDGE,"E10");var subQ1=sQuery(id+"F0.wireOp",EDGE,"E0");var subQ2=makeQuery(id+"F0.imprint","INTERSECT",VERTEX,{"disambiguationData":[OD(0.0)],"derivedFrom":[subQ1,subQ0]});Q10=makeQuery(id+"F0.imprint","IMPRINT",FACE,{"disambiguationData":[TD([[makeQuery(id+"F0.imprint","IMPRINT",EDGE,{"disambiguationData":[TD([[subQ2,-1.0]])],"derivedFrom":subQ1}),-1.0]])]});}
            var Q11;
            {var subQ0=sQuery(id+"F0.wireOp",EDGE,"E10");var subQ1=sQuery(id+"F0.wireOp",EDGE,"E0");var subQ2=makeQuery(id+"F0.imprint","INTERSECT",VERTEX,{"disambiguationData":[OD(0.0)],"derivedFrom":[subQ1,subQ0]});Q11=makeQuery(id+"F0.imprint","IMPRINT",FACE,{"disambiguationData":[TD([[makeQuery(id+"F0.imprint","IMPRINT",EDGE,{"disambiguationData":[TD([[subQ2,-1.0]])],"derivedFrom":subQ1}),1.0]])]});}
            var Q12;
            {var subQ0=sQuery(id+"F0.wireOp",EDGE,"E11.1.0");var subQ1=sQuery(id+"F0.wireOp",EDGE,"E0");var subQ2=makeQuery(id+"F0.imprint","INTERSECT",VERTEX,{"disambiguationData":[OD(0.0)],"derivedFrom":[subQ1,subQ0]});Q12=makeQuery(id+"F0.imprint","IMPRINT",FACE,{"disambiguationData":[TD([[makeQuery(id+"F0.imprint","IMPRINT",EDGE,{"disambiguationData":[TD([[subQ2,-1.0]])],"derivedFrom":subQ1}),1.0]])]});}
            var Q13;
            {var subQ0=sQuery(id+"F0.wireOp",EDGE,"E11.1.0");var subQ1=sQuery(id+"F0.wireOp",EDGE,"E0");var subQ2=makeQuery(id+"F0.imprint","INTERSECT",VERTEX,{"disambiguationData":[OD(0.0)],"derivedFrom":[subQ1,subQ0]});Q13=makeQuery(id+"F0.imprint","IMPRINT",FACE,{"disambiguationData":[TD([[makeQuery(id+"F0.imprint","IMPRINT",EDGE,{"disambiguationData":[TD([[subQ2,-1.0]])],"derivedFrom":subQ1}),-1.0]])]});}
            var Q14;
            {var subQ0=sQuery(id+"F0.wireOp",EDGE,"E11.3.0");var subQ1=sQuery(id+"F0.wireOp",EDGE,"E0");var subQ2=makeQuery(id+"F0.imprint","INTERSECT",VERTEX,{"disambiguationData":[OD(0.0)],"derivedFrom":[subQ1,subQ0]});Q14=makeQuery(id+"F0.imprint","IMPRINT",FACE,{"disambiguationData":[TD([[makeQuery(id+"F0.imprint","IMPRINT",EDGE,{"disambiguationData":[TD([[subQ2,-1.0]])],"derivedFrom":subQ1}),1.0]])]});}
            var Q15;
            {var subQ0=sQuery(id+"F0.wireOp",EDGE,"E11.3.0");var subQ1=sQuery(id+"F0.wireOp",EDGE,"E0");var subQ2=makeQuery(id+"F0.imprint","INTERSECT",VERTEX,{"disambiguationData":[OD(0.0)],"derivedFrom":[subQ1,subQ0]});Q15=makeQuery(id+"F0.imprint","IMPRINT",FACE,{"disambiguationData":[TD([[makeQuery(id+"F0.imprint","IMPRINT",EDGE,{"disambiguationData":[TD([[subQ2,-1.0]])],"derivedFrom":subQ1}),-1.0]])]});}
            var Q16;
            {var subQ0=sQuery(id+"F0.wireOp",EDGE,"E11.4.0");var subQ1=sQuery(id+"F0.wireOp",EDGE,"E0");var subQ2=makeQuery(id+"F0.imprint","INTERSECT",VERTEX,{"disambiguationData":[OD(0.0)],"derivedFrom":[subQ1,subQ0]});Q16=makeQuery(id+"F0.imprint","IMPRINT",FACE,{"disambiguationData":[TD([[makeQuery(id+"F0.imprint","IMPRINT",EDGE,{"disambiguationData":[TD([[subQ2,-1.0]])],"derivedFrom":subQ1}),1.0]])]});}
            var Q17;
            {var subQ0=sQuery(id+"F0.wireOp",EDGE,"E11.4.0");var subQ1=sQuery(id+"F0.wireOp",EDGE,"E0");var subQ2=makeQuery(id+"F0.imprint","INTERSECT",VERTEX,{"disambiguationData":[OD(0.0)],"derivedFrom":[subQ1,subQ0]});Q17=makeQuery(id+"F0.imprint","IMPRINT",FACE,{"disambiguationData":[TD([[makeQuery(id+"F0.imprint","IMPRINT",EDGE,{"disambiguationData":[TD([[subQ2,-1.0]])],"derivedFrom":subQ1}),-1.0]])]});}
            var Q18;
            {var subQ0=sQuery(id+"F0.wireOp",EDGE,"E11.5.0");var subQ1=sQuery(id+"F0.wireOp",EDGE,"E0");var subQ2=makeQuery(id+"F0.imprint","INTERSECT",VERTEX,{"disambiguationData":[OD(0.0)],"derivedFrom":[subQ1,subQ0]});Q18=makeQuery(id+"F0.imprint","IMPRINT",FACE,{"disambiguationData":[TD([[makeQuery(id+"F0.imprint","IMPRINT",EDGE,{"disambiguationData":[TD([[subQ2,-1.0]])],"derivedFrom":subQ1}),-1.0]])]});}
            var Q19;
            {var subQ0=sQuery(id+"F0.wireOp",EDGE,"E11.5.0");var subQ1=sQuery(id+"F0.wireOp",EDGE,"E0");var subQ2=makeQuery(id+"F0.imprint","INTERSECT",VERTEX,{"disambiguationData":[OD(0.0)],"derivedFrom":[subQ1,subQ0]});Q19=makeQuery(id+"F0.imprint","IMPRINT",FACE,{"disambiguationData":[TD([[makeQuery(id+"F0.imprint","IMPRINT",EDGE,{"disambiguationData":[TD([[subQ2,-1.0]])],"derivedFrom":subQ1}),1.0]])]});}
            var Q20;
            {var subQ0=sQuery(id+"F0.wireOp",EDGE,"E12.1.0");var subQ1=sQuery(id+"F0.wireOp",EDGE,"E0");var subQ2=makeQuery(id+"F0.imprint","INTERSECT",VERTEX,{"disambiguationData":[OD(0.0)],"derivedFrom":[subQ1,subQ0]});Q20=makeQuery(id+"F0.imprint","IMPRINT",FACE,{"disambiguationData":[TD([[makeQuery(id+"F0.imprint","IMPRINT",EDGE,{"disambiguationData":[TD([[subQ2,-1.0]])],"derivedFrom":subQ1}),-1.0]])]});}
            var Q21;
            {var subQ0=sQuery(id+"F0.wireOp",EDGE,"E12.4.0");var subQ1=sQuery(id+"F0.wireOp",EDGE,"E0");var subQ2=makeQuery(id+"F0.imprint","INTERSECT",VERTEX,{"disambiguationData":[OD(0.0)],"derivedFrom":[subQ1,subQ0]});Q21=makeQuery(id+"F0.imprint","IMPRINT",FACE,{"disambiguationData":[TD([[makeQuery(id+"F0.imprint","IMPRINT",EDGE,{"disambiguationData":[TD([[subQ2,-1.0]])],"derivedFrom":subQ1}),-1.0]])]});}
            var Q22;
            {var subQ0=sQuery(id+"F0.wireOp",EDGE,"E12.4.0");var subQ1=sQuery(id+"F0.wireOp",EDGE,"E0");var subQ2=makeQuery(id+"F0.imprint","INTERSECT",VERTEX,{"disambiguationData":[OD(0.0)],"derivedFrom":[subQ1,subQ0]});Q22=makeQuery(id+"F0.imprint","IMPRINT",FACE,{"disambiguationData":[TD([[makeQuery(id+"F0.imprint","IMPRINT",EDGE,{"disambiguationData":[TD([[subQ2,-1.0]])],"derivedFrom":subQ1}),1.0]])]});}
            var Q23;
            {var subQ0=sQuery(id+"F0.wireOp",EDGE,"E12.3.0");var subQ1=sQuery(id+"F0.wireOp",EDGE,"E0");var subQ2=makeQuery(id+"F0.imprint","INTERSECT",VERTEX,{"disambiguationData":[OD(0.0)],"derivedFrom":[subQ1,subQ0]});Q23=makeQuery(id+"F0.imprint","IMPRINT",FACE,{"disambiguationData":[TD([[makeQuery(id+"F0.imprint","IMPRINT",EDGE,{"disambiguationData":[TD([[subQ2,-1.0]])],"derivedFrom":subQ1}),-1.0]])]});}
            var Q24;
            {var subQ0=sQuery(id+"F0.wireOp",EDGE,"E12.3.0");var subQ1=sQuery(id+"F0.wireOp",EDGE,"E0");var subQ2=makeQuery(id+"F0.imprint","INTERSECT",VERTEX,{"disambiguationData":[OD(0.0)],"derivedFrom":[subQ1,subQ0]});Q24=makeQuery(id+"F0.imprint","IMPRINT",FACE,{"disambiguationData":[TD([[makeQuery(id+"F0.imprint","IMPRINT",EDGE,{"disambiguationData":[TD([[subQ2,-1.0]])],"derivedFrom":subQ1}),1.0]])]});}
            var Q25;
            {var subQ0=sQuery(id+"F0.wireOp",EDGE,"E12.2.0");var subQ1=sQuery(id+"F0.wireOp",EDGE,"E0");var subQ2=makeQuery(id+"F0.imprint","INTERSECT",VERTEX,{"disambiguationData":[OD(0.0)],"derivedFrom":[subQ1,subQ0]});Q25=makeQuery(id+"F0.imprint","IMPRINT",FACE,{"disambiguationData":[TD([[makeQuery(id+"F0.imprint","IMPRINT",EDGE,{"disambiguationData":[TD([[subQ2,-1.0]])],"derivedFrom":subQ1}),1.0]])]});}
            var Q26;
            {var subQ0=sQuery(id+"F0.wireOp",EDGE,"E12.2.0");var subQ1=sQuery(id+"F0.wireOp",EDGE,"E0");var subQ2=makeQuery(id+"F0.imprint","INTERSECT",VERTEX,{"disambiguationData":[OD(0.0)],"derivedFrom":[subQ1,subQ0]});Q26=makeQuery(id+"F0.imprint","IMPRINT",FACE,{"disambiguationData":[TD([[makeQuery(id+"F0.imprint","IMPRINT",EDGE,{"disambiguationData":[TD([[subQ2,-1.0]])],"derivedFrom":subQ1}),-1.0]])]});}
            var Q27;
            {var subQ0=sQuery(id+"F0.wireOp",EDGE,"E12.5.0");var subQ1=sQuery(id+"F0.wireOp",EDGE,"E0");var subQ2=makeQuery(id+"F0.imprint","INTERSECT",VERTEX,{"disambiguationData":[OD(0.0)],"derivedFrom":[subQ1,subQ0]});Q27=makeQuery(id+"F0.imprint","IMPRINT",FACE,{"disambiguationData":[TD([[makeQuery(id+"F0.imprint","IMPRINT",EDGE,{"disambiguationData":[TD([[subQ2,-1.0]])],"derivedFrom":subQ1}),1.0]])]});}
            var Q28;
            {var subQ0=sQuery(id+"F0.wireOp",EDGE,"E12.1.0");var subQ1=sQuery(id+"F0.wireOp",EDGE,"E0");var subQ2=makeQuery(id+"F0.imprint","INTERSECT",VERTEX,{"disambiguationData":[OD(0.0)],"derivedFrom":[subQ1,subQ0]});Q28=makeQuery(id+"F0.imprint","IMPRINT",FACE,{"disambiguationData":[TD([[makeQuery(id+"F0.imprint","IMPRINT",EDGE,{"disambiguationData":[TD([[subQ2,-1.0]])],"derivedFrom":subQ1}),1.0]])]});}
            extrude(context, id + "F3", {"entities" : qUnion([Q0, Q1, Q2, Q3, Q4, Q5, Q6, Q7, Q8, Q9, Q10, Q11, Q12, Q13, Q14, Q15, Q16, Q17, Q18, Q19, Q20, Q21, Q22, Q23, Q24, Q25, Q26, Q27, Q28]), "operationType" : NewBodyOperationType.REMOVE, "depth" : 25.4 * mm});
        }
        {
            var Q0;
            Q0=makeQuery(id+"F0.imprint","IMPRINT",FACE,{"disambiguationData":[TD([[makeQuery(id+"F0.imprint","IMPRINT",EDGE,{"derivedFrom":sQuery(id+"F0.wireOp",EDGE,"E9.0")}),-1.0]])]});
            extrude(context, id + "F4", {"entities" : qUnion([Q0]), "operationType" : NewBodyOperationType.ADD, "depth" : 38.1 * mm});
        }
    });
